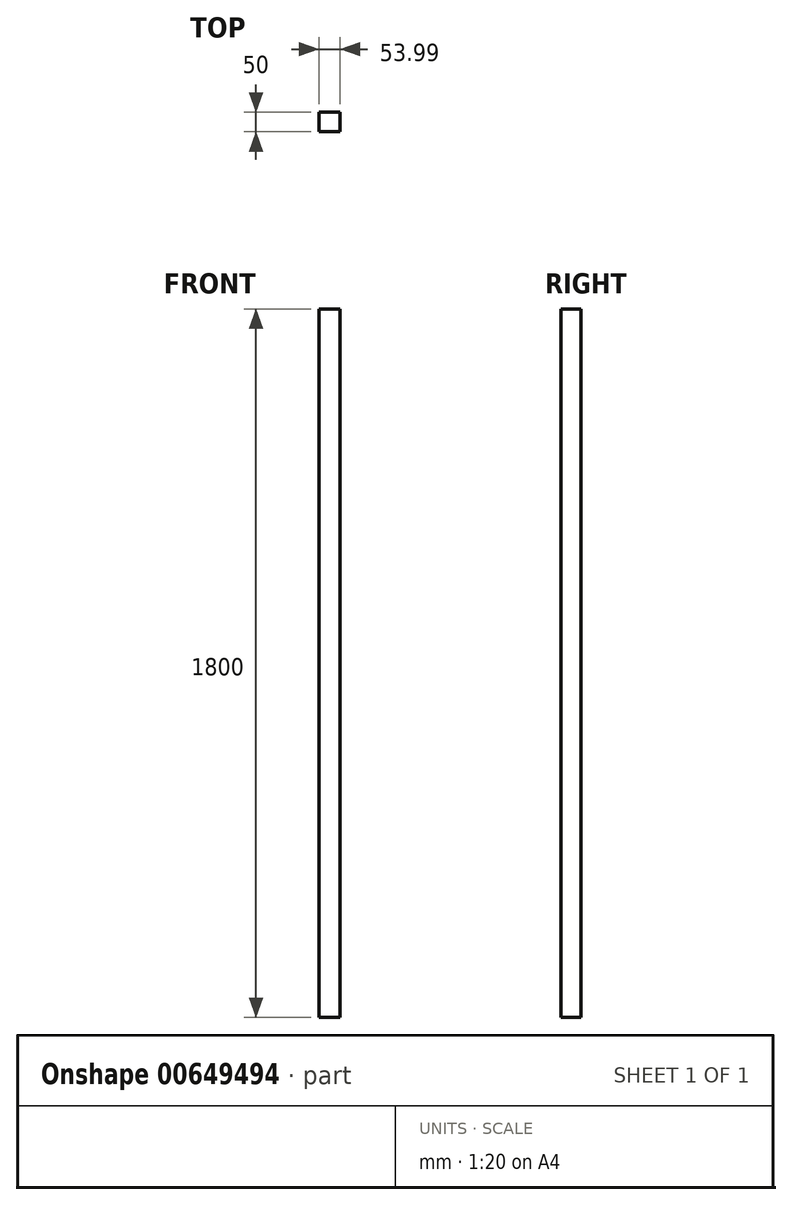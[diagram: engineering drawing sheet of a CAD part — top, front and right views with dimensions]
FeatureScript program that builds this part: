
annotation { "Feature Type Name" : "Feature", "Feature Type Description" : "" }
export const myFeature = defineFeature(function(context is Context, id is Id, definition is map)
    precondition{}
    {
        {
            var Q0;
            Q0=qCreatedBy(makeId("Top.planeOp"),FACE);
            var sketch = newSketch(context, id + "F0", { "sketchPlane" : qUnion([Q0])});
            skLineSegment(sketch, "E0.bottom", {"start": v(0, 0) * mm, "end": v(53.99, 0) * mm});
            skLineSegment(sketch, "E0.top", {"start": v(0, 50) * mm, "end": v(53.99, 50) * mm});
            skLineSegment(sketch, "E0.left", {"start": v(0, 0) * mm, "end": v(0, 50) * mm});
            skLineSegment(sketch, "E0.right", {"start": v(53.99, 0) * mm, "end": v(53.99, 50) * mm});
            skSolve(sketch);
        }
        {
            var Q0;
            Q0=makeQuery(id+"F0.imprint","IMPRINT",FACE,{"disambiguationData":[TD([[makeQuery(id+"F0.imprint","IMPRINT",EDGE,{"derivedFrom":sQuery(id+"F0.wireOp",EDGE,"E0.bottom")}),1.0]])]});
            extrude(context, id + "F1", {"entities" : qUnion([Q0]), "depth" : 1800 * mm, "offsetDistance" : 25 * mm});
        }
    });
